# Revit family: IRISH Curved Head Window with Soldier Course
name_source: partatom
category: Windows
revit_build: Autodesk Revit 2013 (Build: 20120221_2030(x64)
units: mm (PartAtom-declared; Revit-internal decimal feet)

## types (3) — shared parameters
Analytic Construction = <None>
Default Sill Height = 800 mm
Frame depth = 70 mm
Frame width = 20 mm  [stored 0.0656168 ft]
Glass Thickness = 10 mm  [stored 0.0328084 ft]
Material Door = <By Category>
Mullion width = 15 mm  [stored 0.0492126 ft]
Top Panel depth = 600 mm
Wall Closure = By host
Window cill overhang = 50 mm  [stored 0.164042 ft]
Window width = 50 mm  [stored 0.164042 ft]
setback = 65 mm

## per-type parameters (varying)
| type | Construction Type | Height | Material Cill - External | Material Cill - Internal | Material Frame | Material Glazing bead | Material Mullions | Material Window | Width | Window setback |
| Irish 2m x 1.5m |  | 1000 mm  [stored 3.28084 ft] | <By Category> | <By Category> | <By Category> | <By Category> | <By Category> | <By Category> | 1317 mm  [stored 4.32087 ft] | 100 mm  [stored 0.328084 ft] |
| Irish 1 x 1.5 | Aluminium | 1500 mm  [stored 4.92126 ft] | <By Category> | <By Category> | <By Category> | <By Category> | <By Category> | <By Category> | 1000 mm  [stored 3.28084 ft] | 160 mm |
| Curved Head 1317 x 1000 |  | 1000 mm  [stored 3.28084 ft] | Concrete, Precast | Wood - Cherry | Plastic - White | Plastic - White | Plastic - White | Plastic - White | 1200 mm | 135 mm |

note: [stored X ft] marks values corroborated as IEEE doubles in the binary element streams (Revit-internal decimal feet)

## geometry (parser evidence)
native form markers: Blend x6, Sweep x3
no freeform markers — native parametric forms only
